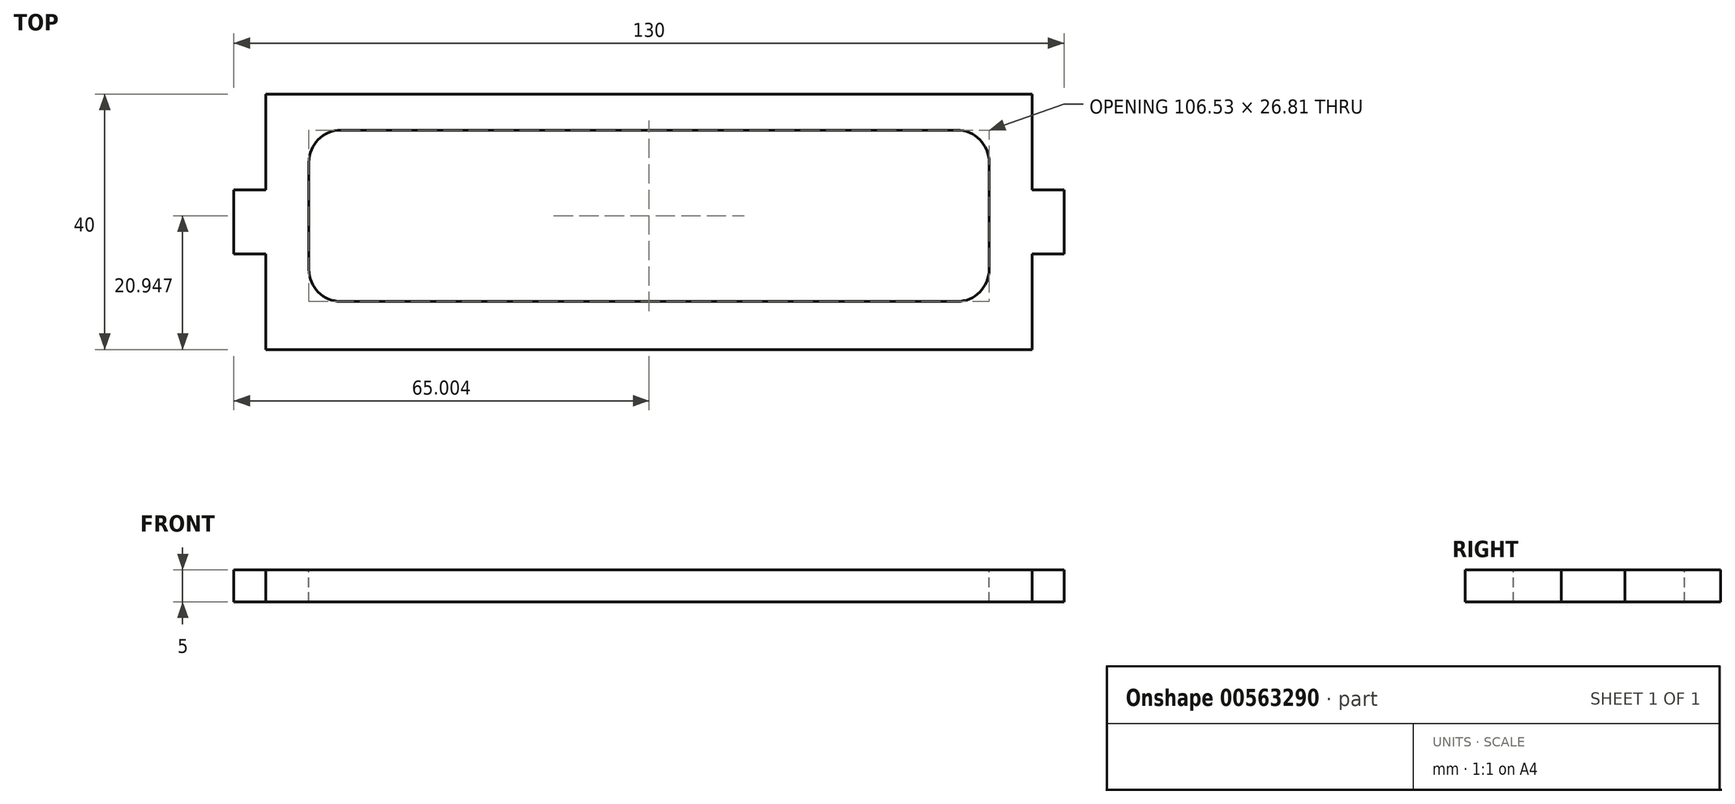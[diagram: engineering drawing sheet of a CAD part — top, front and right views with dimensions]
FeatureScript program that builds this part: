
annotation { "Feature Type Name" : "Feature", "Feature Type Description" : "" }
export const myFeature = defineFeature(function(context is Context, id is Id, definition is map)
    precondition{}
    {
        {
            var Q0;
            Q0=qCreatedBy(makeId("Top.planeOp"),FACE);
            var sketch = newSketch(context, id + "F0", { "sketchPlane" : qUnion([Q0])});
            skLineSegment(sketch, "E0.bottom", {"start": v(-72.89, 25) * mm, "end": v(47.11, 25) * mm});
            skLineSegment(sketch, "E0.top", {"start": v(-72.89, -15) * mm, "end": v(47.11, -15) * mm});
            skLineSegment(sketch, "E0.left", {"start": v(-72.89, 25) * mm, "end": v(-72.89, 10) * mm});
            skLineSegment(sketch, "E0.right", {"start": v(47.11, 25) * mm, "end": v(47.11, 10) * mm});
            skLineSegment(sketch, "E1.bottom", {"start": v(47.11, 10) * mm, "end": v(52.11, 10) * mm});
            skLineSegment(sketch, "E1.top", {"start": v(47.11, 0) * mm, "end": v(52.11, 0) * mm});
            skLineSegment(sketch, "E1.right", {"start": v(52.11, 10) * mm, "end": v(52.11, 0) * mm});
            skLineSegment(sketch, "E2.bottom", {"start": v(-72.89, 10) * mm, "end": v(-77.89, 10) * mm});
            skLineSegment(sketch, "E2.top", {"start": v(-72.89, 0) * mm, "end": v(-77.89, 0) * mm});
            skLineSegment(sketch, "E2.right", {"start": v(-77.89, 10) * mm, "end": v(-77.89, 0) * mm});
            skLineSegment(sketch, "E3.trimOffspring", {"start": v(-72.89, 0) * mm, "end": v(-72.89, -15) * mm});
            skLineSegment(sketch, "E4.trimOffspring", {"start": v(47.11, 0) * mm, "end": v(47.11, -15) * mm});
            skLineSegment(sketch, "E5.bottom", {"start": v(-57.4, 15.95) * mm, "end": v(-27.4, 15.95) * mm});
            skLineSegment(sketch, "E5.top", {"start": v(-57.4, -4.05) * mm, "end": v(-27.4, -4.05) * mm});
            skLineSegment(sketch, "E5.left", {"start": v(-62.4, 10.95) * mm, "end": v(-62.4, 0.95) * mm});
            skLineSegment(sketch, "E5.right", {"start": v(-22.4, 10.95) * mm, "end": v(-22.4, 0.95) * mm});
            skLineSegment(sketch, "E6.left", {"start": v(-22.4, -4.05) * mm, "end": v(-22.4, 15.95) * mm});
            skLineSegment(sketch, "E6.right", {"start": v(-2.4, 0.95) * mm, "end": v(-2.4, 10.95) * mm});
            skLineSegment(sketch, "E7.bottom", {"start": v(2.6, 15.95) * mm, "end": v(32.6, 15.95) * mm});
            skLineSegment(sketch, "E7.top", {"start": v(2.6, -4.05) * mm, "end": v(32.6, -4.05) * mm});
            skLineSegment(sketch, "E7.left", {"start": v(-2.4, 15.95) * mm, "end": v(-2.4, -4.05) * mm});
            skLineSegment(sketch, "E7.right", {"start": v(37.6, 10.95) * mm, "end": v(37.6, 0.95) * mm});
            skPoint(sketch, "E8.visualSharp", {"position": v(-62.4, 15.95) * mm});
            skArc(sketch, "E8.filletArc", {"start": v(-57.4, 15.95) * mm, "mid": v(-60.94, 14.48) * mm, "end": v(-62.4, 10.95) * mm});
            skPoint(sketch, "E9.visualSharp", {"position": v(-62.4, -4.05) * mm});
            skArc(sketch, "E9.filletArc", {"start": v(-62.4, 0.95) * mm, "mid": v(-60.94, -2.59) * mm, "end": v(-57.4, -4.05) * mm});
            skPoint(sketch, "E10.visualSharp", {"position": v(-22.4, 15.95) * mm});
            skArc(sketch, "E10.filletArc", {"start": v(-24.46, 15) * mm, "mid": v(-25.86, 15.7) * mm, "end": v(-27.4, 15.95) * mm});
            skPoint(sketch, "E11.visualSharp", {"position": v(-22.4, 10.95) * mm});
            skArc(sketch, "E11.filletArc", {"start": v(-22.4, 10.95) * mm, "mid": v(-22.95, 13.22) * mm, "end": v(-24.46, 15) * mm});
            skPoint(sketch, "E12.visualSharp", {"position": v(-22.4, -4.05) * mm});
            skArc(sketch, "E12.filletArc", {"start": v(-27.4, -4.05) * mm, "mid": v(-23.87, -2.59) * mm, "end": v(-22.4, 0.95) * mm});
            skPoint(sketch, "E13.visualSharp", {"position": v(-2.4, 15.95) * mm});
            skArc(sketch, "E13.filletArc", {"start": v(2.6, 15.95) * mm, "mid": v(-0.94, 14.48) * mm, "end": v(-2.4, 10.95) * mm});
            skPoint(sketch, "E14.visualSharp", {"position": v(-2.4, -4.05) * mm});
            skArc(sketch, "E14.filletArc", {"start": v(-2.4, 0.95) * mm, "mid": v(-0.94, -2.59) * mm, "end": v(2.6, -4.05) * mm});
            skPoint(sketch, "E15.visualSharp", {"position": v(37.6, 15.95) * mm});
            skArc(sketch, "E15.filletArc", {"start": v(37.6, 10.95) * mm, "mid": v(36.13, 14.48) * mm, "end": v(32.6, 15.95) * mm});
            skPoint(sketch, "E16.visualSharp", {"position": v(37.6, -4.05) * mm});
            skArc(sketch, "E16.filletArc", {"start": v(32.6, -4.05) * mm, "mid": v(36.13, -2.59) * mm, "end": v(37.6, 0.95) * mm});
            skSolve(sketch);
        }
        {
            var Q0;
            Q0 = qSketchRegion(id + "F0", true);
            extrude(context, id + "F1", {"entities" : qUnion([Q0]), "depth" : 5 * mm, "offsetDistance" : 25 * mm});
        }
        {
            var Q0;
            Q0=makeQuery(id+"F1.opExtrude","CAP_FACE",FACE,{"disambiguationData":[OSD([sQuery(id+"F0.wireOp",EDGE,"E0.bottom"),sQuery(id+"F0.wireOp",EDGE,"E0.top"),sQuery(id+"F0.wireOp",EDGE,"E0.left"),sQuery(id+"F0.wireOp",EDGE,"E0.right"),sQuery(id+"F0.wireOp",EDGE,"E1.bottom"),sQuery(id+"F0.wireOp",EDGE,"E1.top"),sQuery(id+"F0.wireOp",EDGE,"E1.right"),sQuery(id+"F0.wireOp",EDGE,"E2.bottom"),sQuery(id+"F0.wireOp",EDGE,"E2.top"),sQuery(id+"F0.wireOp",EDGE,"E2.right"),sQuery(id+"F0.wireOp",EDGE,"E3.trimOffspring"),sQuery(id+"F0.wireOp",EDGE,"E4.trimOffspring"),sQuery(id+"F0.wireOp",EDGE,"E5.bottom"),sQuery(id+"F0.wireOp",EDGE,"E5.top"),sQuery(id+"F0.wireOp",EDGE,"E5.left"),sQuery(id+"F0.wireOp",EDGE,"E6.left"),sQuery(id+"F0.wireOp",EDGE,"E7.bottom"),sQuery(id+"F0.wireOp",EDGE,"E7.top"),sQuery(id+"F0.wireOp",EDGE,"E7.left"),sQuery(id+"F0.wireOp",EDGE,"E7.right"),sQuery(id+"F0.wireOp",EDGE,"E8.filletArc"),sQuery(id+"F0.wireOp",EDGE,"E9.filletArc"),sQuery(id+"F0.wireOp",EDGE,"E10.filletArc"),sQuery(id+"F0.wireOp",EDGE,"E11.filletArc"),sQuery(id+"F0.wireOp",EDGE,"E12.filletArc"),sQuery(id+"F0.wireOp",EDGE,"E13.filletArc"),sQuery(id+"F0.wireOp",EDGE,"E14.filletArc"),sQuery(id+"F0.wireOp",EDGE,"E15.filletArc"),sQuery(id+"F0.wireOp",EDGE,"E16.filletArc")])],"isStart":false});
            var sketch = newSketch(context, id + "F2", { "sketchPlane" : qUnion([Q0])});
            skLineSegment(sketch, "E17.bottom", {"start": v(35.38, 19.35) * mm, "end": v(-61.15, 19.35) * mm});
            skLineSegment(sketch, "E17.top", {"start": v(35.38, -7.46) * mm, "end": v(-61.15, -7.46) * mm});
            skLineSegment(sketch, "E17.left", {"start": v(40.38, 14.35) * mm, "end": v(40.38, -2.46) * mm});
            skLineSegment(sketch, "E17.right", {"start": v(-66.15, 14.35) * mm, "end": v(-66.15, -2.46) * mm});
            skPoint(sketch, "E17.middle", {"position": v(-12.89, 5.95) * mm});
            skPoint(sketch, "E17.middle.positionSnap0", {"position": v(-2.4, 5.95) * mm});
            skPoint(sketch, "E17.middle.positionSnap1", {"position": v(-12.89, 25) * mm});
            skPoint(sketch, "E17.centerSnap0", {"position": v(-2.4, 5.95) * mm});
            skPoint(sketch, "E17.centerSnap1", {"position": v(-12.89, 25) * mm});
            skPoint(sketch, "E18.visualSharp", {"position": v(40.38, 19.35) * mm});
            skArc(sketch, "E18.filletArc", {"start": v(40.38, 14.35) * mm, "mid": v(38.91, 17.89) * mm, "end": v(35.38, 19.35) * mm});
            skPoint(sketch, "E19.visualSharp", {"position": v(40.38, -7.46) * mm});
            skArc(sketch, "E19.filletArc", {"start": v(35.38, -7.46) * mm, "mid": v(38.91, -6) * mm, "end": v(40.38, -2.46) * mm});
            skPoint(sketch, "E20.visualSharp", {"position": v(-66.15, -7.46) * mm});
            skArc(sketch, "E20.filletArc", {"start": v(-66.15, -2.46) * mm, "mid": v(-64.69, -6) * mm, "end": v(-61.15, -7.46) * mm});
            skPoint(sketch, "E21.visualSharp", {"position": v(-66.15, 19.35) * mm});
            skArc(sketch, "E21.filletArc", {"start": v(-61.15, 19.35) * mm, "mid": v(-64.69, 17.89) * mm, "end": v(-66.15, 14.35) * mm});
            skSolve(sketch);
        }
        {
            var Q0;
            Q0=makeQuery(id+"F2.imprint","IMPRINT",FACE,{"disambiguationData":[TD([[makeQuery(id+"F2.imprint","IMPRINT",EDGE,{"derivedFrom":sQuery(id+"F2.wireOp",EDGE,"E17.bottom")}),1.0]])]});
            extrude(context, id + "F3", {"entities" : qUnion([Q0]), "operationType" : NewBodyOperationType.REMOVE, "oppositeDirection" : true, "depth" : 25 * mm, "offsetDistance" : 25 * mm});
        }
    });
